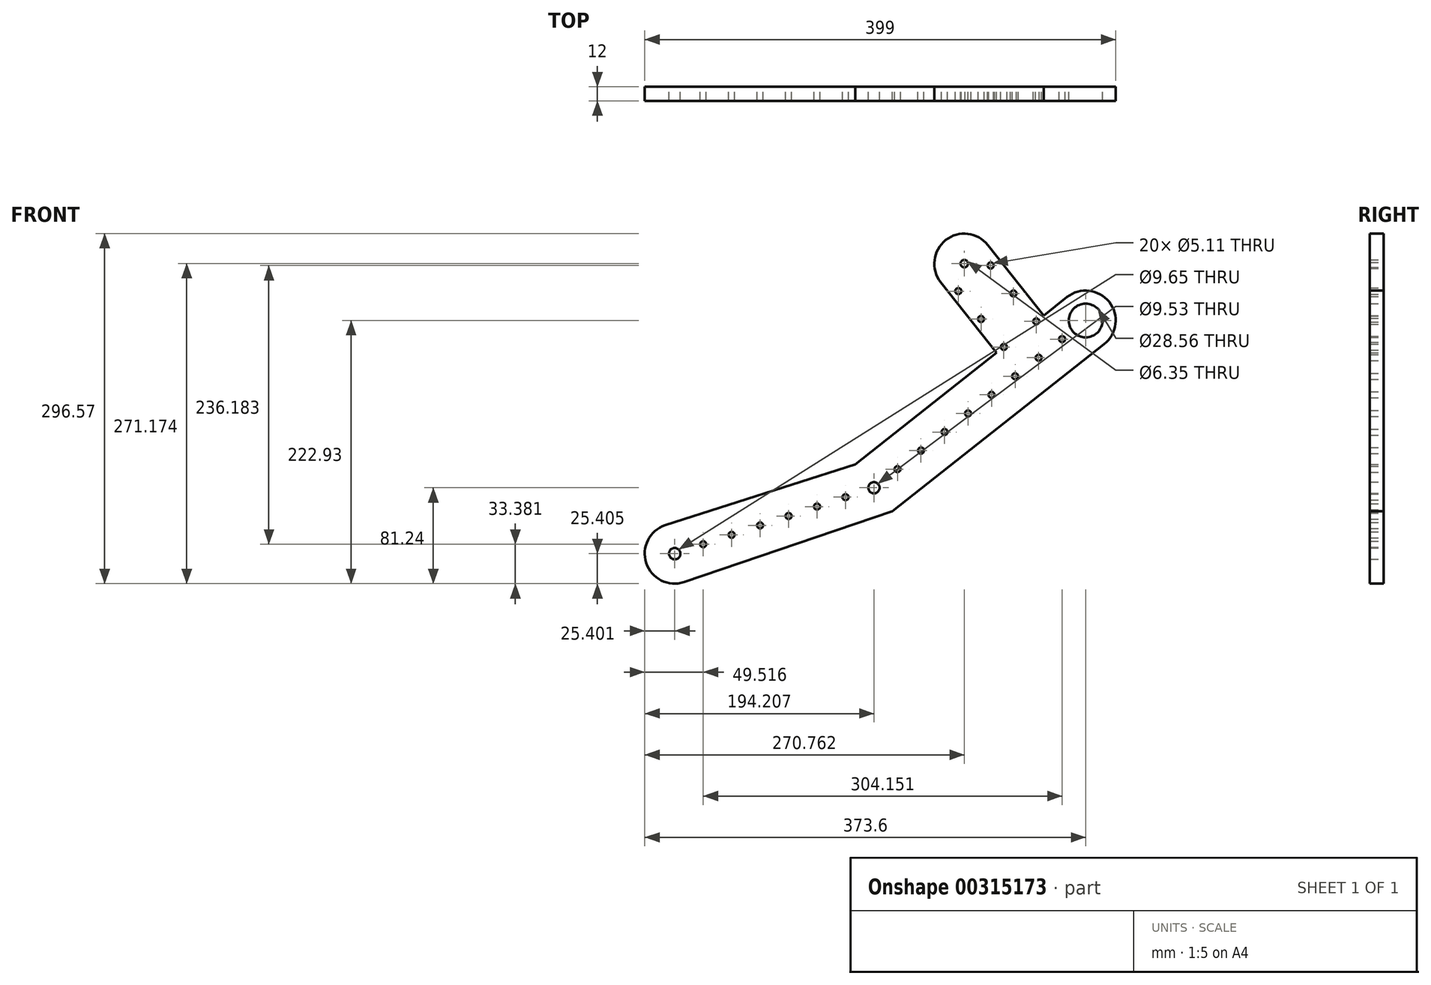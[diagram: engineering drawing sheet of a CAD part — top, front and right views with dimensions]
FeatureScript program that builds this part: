
annotation { "Feature Type Name" : "Feature", "Feature Type Description" : "" }
export const myFeature = defineFeature(function(context is Context, id is Id, definition is map)
    precondition{}
    {
        {
            var Q0;
            Q0=qCreatedBy(makeId("Front.planeOp"),FACE);
            var sketch = newSketch(context, id + "F0", { "sketchPlane" : qUnion([Q0])});
            skLineSegment(sketch, "E0", {"start": v(-1270, 0) * mm, "end": v(1270, 0) * mm, "construction": true});
            skLineSegment(sketch, "E1.bottom", {"start": v(317.5, 25.4) * mm, "end": v(-317.5, 25.4) * mm, "construction": true});
            skLineSegment(sketch, "E1.top", {"start": v(317.5, 76.2) * mm, "end": v(-317.5, 76.2) * mm, "construction": true});
            skLineSegment(sketch, "E1.left", {"start": v(317.5, 25.4) * mm, "end": v(317.5, 76.2) * mm, "construction": true});
            skLineSegment(sketch, "E1.right", {"start": v(-317.5, 25.4) * mm, "end": v(-317.5, 76.2) * mm, "construction": true});
            skPoint(sketch, "E1.middle", {"position": v(0, 50.8) * mm});
            skCircle(sketch, "E2", {"center": v(0, 50.8) * mm, "radius": 50.8 * mm, "construction": true});
            skCircle(sketch, "E3", {"center": v(228.6, 50.8) * mm, "radius": 50.8 * mm, "construction": true});
            skCircle(sketch, "E4", {"center": v(-228.6, 50.8) * mm, "radius": 50.8 * mm, "construction": true});
            skLineSegment(sketch, "E5", {"start": v(-228.6, 50.8) * mm, "end": v(-228.6, 254) * mm, "construction": true});
            skLineSegment(sketch, "E6", {"start": v(-228.6, 254) * mm, "end": v(-408, 112.31) * mm, "construction": true});
            skLineSegment(sketch, "E7", {"start": v(-408, 112.31) * mm, "end": v(-576.8, 56.47) * mm, "construction": true});
            skLineSegment(sketch, "E8", {"start": v(-698.5, 0) * mm, "end": v(-698.5, 762) * mm, "construction": true});
            skCircle(sketch, "E9", {"center": v(-576.8, 56.47) * mm, "radius": 4.83 * mm});
            skCircle(sketch, "E10", {"center": v(-408, 112.31) * mm, "radius": 4.76 * mm});
            skCircle(sketch, "E11", {"center": v(-228.6, 254) * mm, "radius": 14.28 * mm});
            skLineSegment(sketch, "E12", {"start": v(-268.47, 222.51) * mm, "end": v(-331.44, 302.24) * mm, "construction": true});
            skLineSegment(sketch, "E13.bottom", {"start": v(-698.5, 0) * mm, "end": v(-419.1, 0) * mm});
            skLineSegment(sketch, "E13.top", {"start": v(-698.5, 35.56) * mm, "end": v(-419.1, 35.56) * mm, "construction": true});
            skLineSegment(sketch, "E13.left", {"start": v(-698.5, 0) * mm, "end": v(-698.5, 35.56) * mm});
            skLineSegment(sketch, "E13.right", {"start": v(-419.1, 0) * mm, "end": v(-419.1, 35.56) * mm, "construction": true});
            skLineSegment(sketch, "E14", {"start": v(-584.78, 80.59) * mm, "end": v(-568.82, 32.36) * mm, "construction": true});
            skArc(sketch, "E15", {"start": v(-584.78, 80.59) * mm, "mid": v(-600.91, 48.5) * mm, "end": v(-568.82, 32.36) * mm});
            skLineSegment(sketch, "E16", {"start": v(-423.74, 132.24) * mm, "end": v(-392.25, 92.38) * mm, "construction": true});
            skLineSegment(sketch, "E17", {"start": v(-584.78, 80.59) * mm, "end": v(-423.74, 132.24) * mm});
            skLineSegment(sketch, "E18", {"start": v(-568.82, 32.36) * mm, "end": v(-392.25, 92.38) * mm});
            skLineSegment(sketch, "E19", {"start": v(-244.34, 273.93) * mm, "end": v(-212.86, 234.07) * mm, "construction": true});
            skLineSegment(sketch, "E20", {"start": v(-244.34, 273.93) * mm, "end": v(-423.74, 132.24) * mm, "construction": true});
            skLineSegment(sketch, "E21", {"start": v(-392.25, 92.38) * mm, "end": v(-212.86, 234.07) * mm});
            skArc(sketch, "E22", {"start": v(-212.86, 234.07) * mm, "mid": v(-208.67, 269.74) * mm, "end": v(-244.34, 273.93) * mm});
            skCircle(sketch, "E23", {"center": v(-552.68, 64.45) * mm, "radius": 2.55 * mm});
            skCircle(sketch, "E24.1.0.0", {"center": v(-528.57, 72.43) * mm, "radius": 2.55 * mm});
            skCircle(sketch, "E24.2.0.0", {"center": v(-504.45, 80.4) * mm, "radius": 2.55 * mm});
            skCircle(sketch, "E24.3.0.0", {"center": v(-480.34, 88.38) * mm, "radius": 2.55 * mm});
            skCircle(sketch, "E24.4.0.0", {"center": v(-456.22, 96.36) * mm, "radius": 2.55 * mm});
            skCircle(sketch, "E24.5.0.0", {"center": v(-432.1, 104.33) * mm, "radius": 2.55 * mm});
            skLineSegment(sketch, "E24.direction1", {"start": v(-552.68, 64.45) * mm, "end": v(-528.57, 72.43) * mm, "construction": true});
            skLineSegment(sketch, "E25", {"start": v(-432.1, 104.33) * mm, "end": v(-552.68, 64.45) * mm, "construction": true});
            skCircle(sketch, "E26", {"center": v(-388.06, 128.05) * mm, "radius": 2.55 * mm});
            skCircle(sketch, "E27.1.0.0", {"center": v(-368.13, 143.8) * mm, "radius": 2.55 * mm});
            skCircle(sketch, "E27.2.0.0", {"center": v(-348.2, 159.54) * mm, "radius": 2.55 * mm});
            skCircle(sketch, "E27.3.0.0", {"center": v(-328.26, 175.28) * mm, "radius": 2.55 * mm});
            skCircle(sketch, "E27.4.0.0", {"center": v(-308.33, 191.03) * mm, "radius": 2.55 * mm});
            skCircle(sketch, "E27.5.0.0", {"center": v(-288.4, 206.77) * mm, "radius": 2.55 * mm});
            skCircle(sketch, "E27.6.0.0", {"center": v(-268.47, 222.51) * mm, "radius": 2.55 * mm});
            skCircle(sketch, "E27.7.0.0", {"center": v(-248.53, 238.26) * mm, "radius": 2.55 * mm});
            skLineSegment(sketch, "E27.direction1", {"start": v(-388.06, 128.05) * mm, "end": v(-368.13, 143.8) * mm, "construction": true});
            skLineSegment(sketch, "E28", {"start": v(-248.53, 238.26) * mm, "end": v(-388.06, 128.05) * mm, "construction": true});
            skLineSegment(sketch, "E29", {"start": v(-351.37, 286.5) * mm, "end": v(-311.5, 317.99) * mm, "construction": true});
            skArc(sketch, "E30", {"start": v(-311.5, 317.99) * mm, "mid": v(-347.18, 322.18) * mm, "end": v(-351.37, 286.5) * mm});
            skCircle(sketch, "E31", {"center": v(-331.44, 302.24) * mm, "radius": 3.18 * mm});
            skLineSegment(sketch, "E32", {"start": v(-311.5, 317.99) * mm, "end": v(-264.28, 258.19) * mm});
            skLineSegment(sketch, "E33", {"start": v(-351.37, 286.5) * mm, "end": v(-304.14, 226.7) * mm});
            skLineSegment(sketch, "E34", {"start": v(-264.28, 258.19) * mm, "end": v(-244.34, 273.93) * mm});
            skLineSegment(sketch, "E35", {"start": v(-423.74, 132.24) * mm, "end": v(-304.14, 226.7) * mm});
            skLineSegment(sketch, "E36", {"start": v(-331.44, 302.24) * mm, "end": v(133.99, 152.4) * mm, "construction": true});
            skCircle(sketch, "E37", {"center": v(-297.94, 231.6) * mm, "radius": 2.55 * mm});
            skCircle(sketch, "E38", {"center": v(-270.48, 253.3) * mm, "radius": 2.55 * mm});
            skLineSegment(sketch, "E39", {"start": v(-297.94, 231.6) * mm, "end": v(-270.48, 253.3) * mm, "construction": true});
            skPoint(sketch, "E40", {"position": v(-284.2, 242.45) * mm});
            skCircle(sketch, "E41.0.1.0", {"center": v(-289.78, 276.96) * mm, "radius": 2.55 * mm});
            skCircle(sketch, "E41.0.1.1", {"center": v(-317.25, 255.27) * mm, "radius": 2.55 * mm});
            skCircle(sketch, "E41.0.2.0", {"center": v(-309.08, 300.63) * mm, "radius": 2.55 * mm});
            skCircle(sketch, "E41.0.2.1", {"center": v(-336.55, 278.94) * mm, "radius": 2.55 * mm});
            skLineSegment(sketch, "E41.direction1", {"start": v(-297.94, 231.6) * mm, "end": v(-278.71, 231.6) * mm, "construction": true});
            skLineSegment(sketch, "E41.direction2", {"start": v(-297.94, 231.6) * mm, "end": v(-317.25, 255.27) * mm, "construction": true});
            skSolve(sketch);
        }
        {
            var Q0;
            Q0 = qSketchRegion(id + "F0", true);
            extrude(context, id + "F1", {"entities" : qUnion([Q0]), "depth" : 12 * mm});
        }
    });
